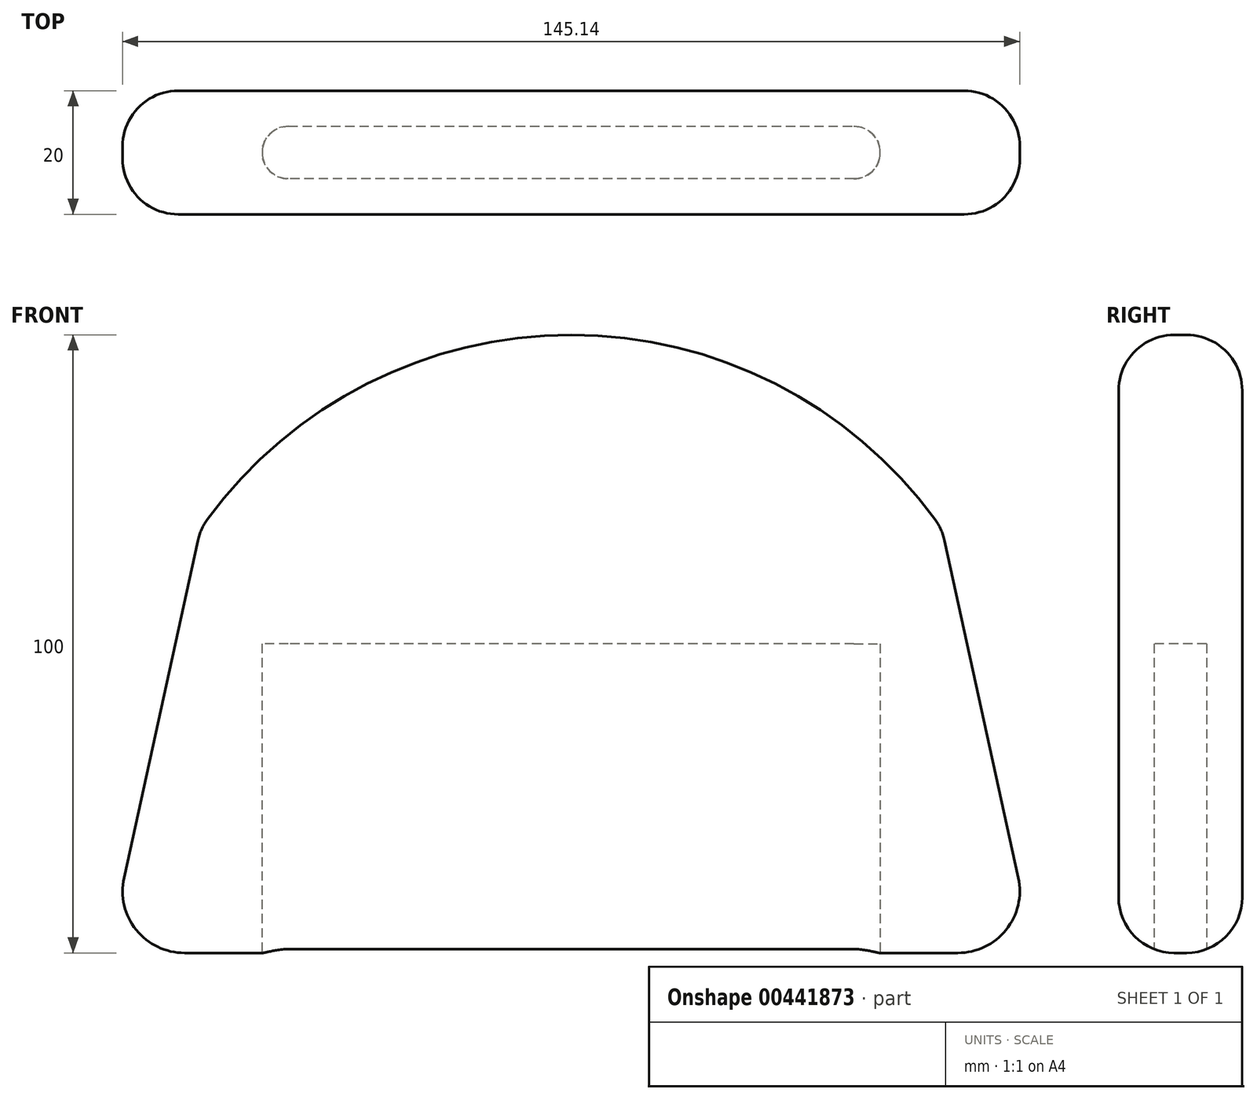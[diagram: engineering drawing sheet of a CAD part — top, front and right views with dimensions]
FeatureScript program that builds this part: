
annotation { "Feature Type Name" : "Feature", "Feature Type Description" : "" }
export const myFeature = defineFeature(function(context is Context, id is Id, definition is map)
    precondition{}
    {
        {
            var Q0;
            Q0=qCreatedBy(makeId("Front.planeOp"),FACE);
            var sketch = newSketch(context, id + "F0", { "sketchPlane" : qUnion([Q0])});
            skLineSegment(sketch, "E0.bottom", {"start": v(12.43, 0) * mm, "end": v(137.57, 0) * mm});
            skLineSegment(sketch, "E0.left", {"start": v(2.66, 12.14) * mm, "end": v(15, 68.54) * mm});
            skLineSegment(sketch, "E0.right", {"start": v(147.34, 12.14) * mm, "end": v(135, 68.54) * mm});
            skLineSegment(sketch, "E1", {"start": v(75, 100) * mm, "end": v(75, 255.47) * mm, "construction": true});
            skArc(sketch, "E2", {"start": v(135, 68.54) * mm, "mid": v(75, 100) * mm, "end": v(15, 68.54) * mm});
            skPoint(sketch, "E3.MirrorCS.end.orphan", {"position": v(75, 116.67) * mm});
            skPoint(sketch, "E3.MirrorCS.start.orphan", {"position": v(102.86, 116.67) * mm});
            skPoint(sketch, "E4.end.orphan", {"position": v(47.14, 116.67) * mm});
            skLineSegment(sketch, "E5", {"start": v(15, 68.54) * mm, "end": v(135, 68.54) * mm, "construction": true});
            skPoint(sketch, "E6", {"position": v(75, 0) * mm});
            skPoint(sketch, "E7.visualSharp", {"position": v(0, 0) * mm});
            skArc(sketch, "E7.filletArc", {"start": v(2.66, 12.14) * mm, "mid": v(4.63, 3.73) * mm, "end": v(12.43, 0) * mm});
            skPoint(sketch, "E8.visualSharp", {"position": v(150, 0) * mm});
            skArc(sketch, "E8.filletArc", {"start": v(137.57, 0) * mm, "mid": v(145.37, 3.73) * mm, "end": v(147.34, 12.14) * mm});
            skSolve(sketch);
        }
        {
            var Q0;
            Q0=makeQuery(id+"F0.imprint","IMPRINT",FACE,{"disambiguationData":[TD([[makeQuery(id+"F0.imprint","IMPRINT",EDGE,{"derivedFrom":sQuery(id+"F0.wireOp",EDGE,"E0.top")}),1.0]])]});
            var Q1;
            Q1=makeQuery(id+"F0.imprint","IMPRINT",FACE,{"disambiguationData":[TD([[makeQuery(id+"F0.imprint","IMPRINT",EDGE,{"derivedFrom":sQuery(id+"F0.wireOp",EDGE,"E0.bottom")}),1.0]])]});
            extrude(context, id + "F1", {"entities" : qUnion([Q0, Q1]), "depth" : 20 * mm, "offsetDistance" : 25 * mm});
        }
        {
            var Q0;
            Q0=makeQuery(id+"F1.opExtrude","CAP_EDGE",EDGE,{"disambiguationData":[OSD([sQuery(id+"F0.wireOp",EDGE,"E0.left")])],"isStart":false});
            var Q1;
            Q1=makeQuery(id+"F1.opExtrude","CAP_EDGE",EDGE,{"disambiguationData":[OSD([sQuery(id+"F0.wireOp",EDGE,"E0.left")])],"isStart":true});
            var Q2;
            Q2=makeQuery(id+"F1.opExtrude","CAP_EDGE",EDGE,{"disambiguationData":[OSD([sQuery(id+"F0.wireOp",EDGE,"E0.right")])],"isStart":false});
            var Q3;
            Q3=makeQuery(id+"F1.opExtrude","CAP_EDGE",EDGE,{"disambiguationData":[OSD([sQuery(id+"F0.wireOp",EDGE,"E0.right")])],"isStart":true});
            var Q4;
            Q4=makeQuery(id+"F1.opExtrude","CAP_FACE",FACE,{"disambiguationData":[OSD([sQuery(id+"F0.wireOp",EDGE,"E0.bottom"),sQuery(id+"F0.wireOp",EDGE,"E0.left"),sQuery(id+"F0.wireOp",EDGE,"E0.right"),sQuery(id+"F0.wireOp",EDGE,"E2")])],"isStart":false});
            var Q5;
            Q5=makeQuery(id+"F1.opExtrude","CAP_EDGE",EDGE,{"disambiguationData":[OSD([sQuery(id+"F0.wireOp",EDGE,"E2")])],"isStart":true});
            var Q6;
            Q6=makeQuery(id+"F1.opExtrude","SWEPT_EDGE",EDGE,{"disambiguationData":[OSD([sQuery(id+"F0.wireOp",EDGE,"E0.top"),sQuery(id+"F0.wireOp",EDGE,"E0.left"),sQuery(id+"F0.wireOp",EDGE,"E2")])]});
            var Q7;
            Q7=makeQuery(id+"F1.opExtrude","SWEPT_EDGE",EDGE,{"disambiguationData":[OSD([sQuery(id+"F0.wireOp",EDGE,"E0.top"),sQuery(id+"F0.wireOp",EDGE,"E0.right"),sQuery(id+"F0.wireOp",EDGE,"E2")])]});
            fillet(context, id + "F2", {"entities" : qUnion([Q0, Q1, Q2, Q3, Q4, Q5, Q6, Q7]), "radius" : 9 * mm, "tangentPropagation" : true, "allowEdgeOverflow" : false});
        }
        {
            var Q0;
            Q0=makeQuery(id+"F1.opExtrude","SWEPT_FACE",FACE,{"disambiguationData":[OSD([sQuery(id+"F0.wireOp",EDGE,"E0.bottom")])]});
            var sketch = newSketch(context, id + "F3", { "sketchPlane" : qUnion([Q0])});
            skLineSegment(sketch, "E9", {"start": v(0, 10) * mm, "end": v(150, 10) * mm, "construction": true});
            skLineSegment(sketch, "E10.bottom", {"start": v(120.75, 5.75) * mm, "end": v(29.25, 5.75) * mm});
            skLineSegment(sketch, "E10.top", {"start": v(120.75, 14.25) * mm, "end": v(29.25, 14.25) * mm});
            skPoint(sketch, "E10.middle", {"position": v(75, 10) * mm});
            skArc(sketch, "E11", {"start": v(29.25, 14.25) * mm, "mid": v(25, 10) * mm, "end": v(29.25, 5.75) * mm});
            skArc(sketch, "E12", {"start": v(120.75, 5.75) * mm, "mid": v(125, 10) * mm, "end": v(120.75, 14.25) * mm});
            skSolve(sketch);
        }
        {
            var Q0;
            Q0 = qSketchRegion(id + "F3", true);
            extrude(context, id + "F4", {"entities" : qUnion([Q0]), "operationType" : NewBodyOperationType.REMOVE, "oppositeDirection" : true, "depth" : 50 * mm, "offsetDistance" : 25 * mm});
        }
    });
